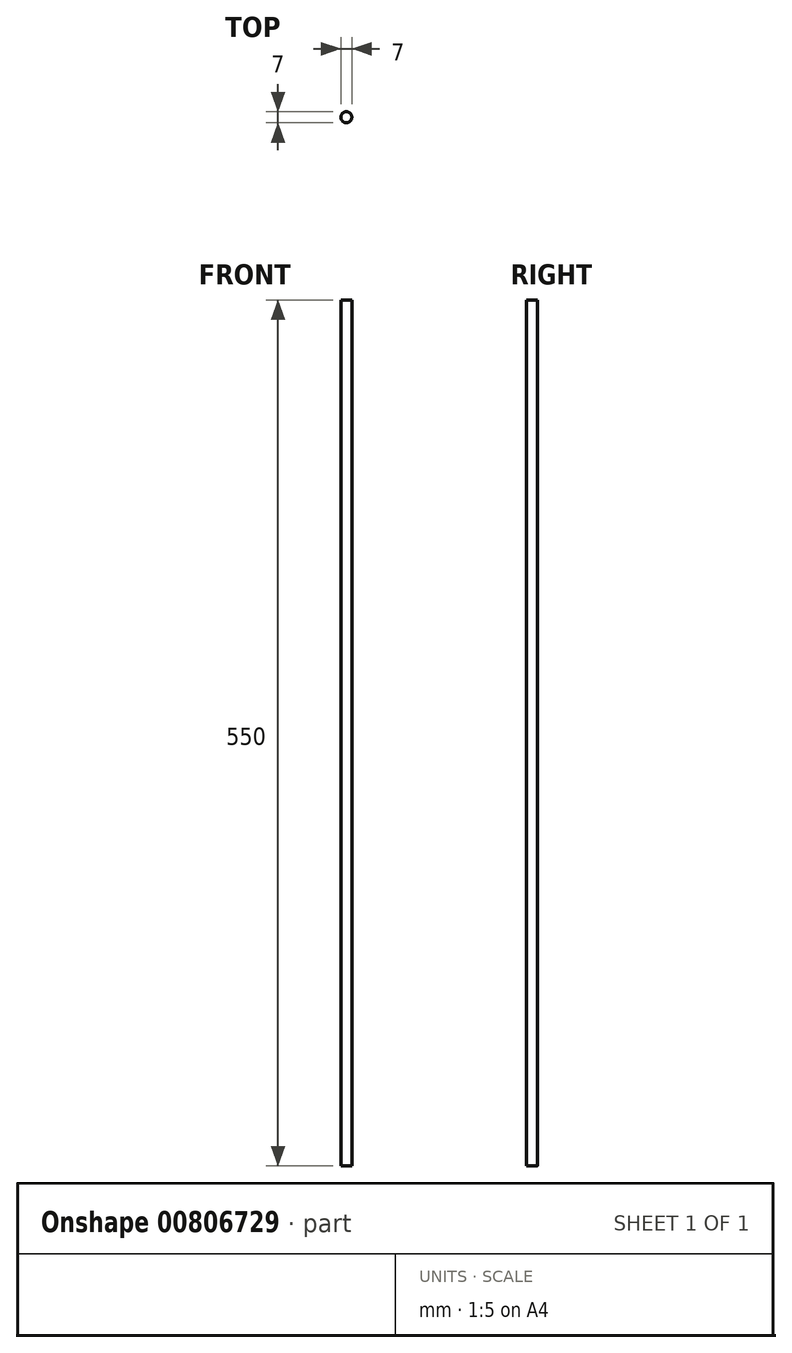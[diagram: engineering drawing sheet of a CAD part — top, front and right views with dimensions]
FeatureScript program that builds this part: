
annotation { "Feature Type Name" : "Feature", "Feature Type Description" : "" }
export const myFeature = defineFeature(function(context is Context, id is Id, definition is map)
    precondition{}
    {
        {
            var Q0;
            Q0=qCreatedBy(makeId("Top.planeOp"),FACE);
            var sketch = newSketch(context, id + "F0", { "sketchPlane" : qUnion([Q0])});
            skCircle(sketch, "E0", {"center": v(0, 0) * mm, "radius": 3.5 * mm});
            skSolve(sketch);
        }
        {
            var Q0;
            Q0=makeQuery(id+"F0.imprint","IMPRINT",FACE,{"disambiguationData":[TD([[makeQuery(id+"F0.imprint","IMPRINT",EDGE,{"derivedFrom":sQuery(id+"F0.wireOp",EDGE,"E0")}),1.0]])]});
            extrude(context, id + "F1", {"entities" : qUnion([Q0]), "depth" : 550 * mm, "offsetDistance" : 25 * mm});
        }
    });
